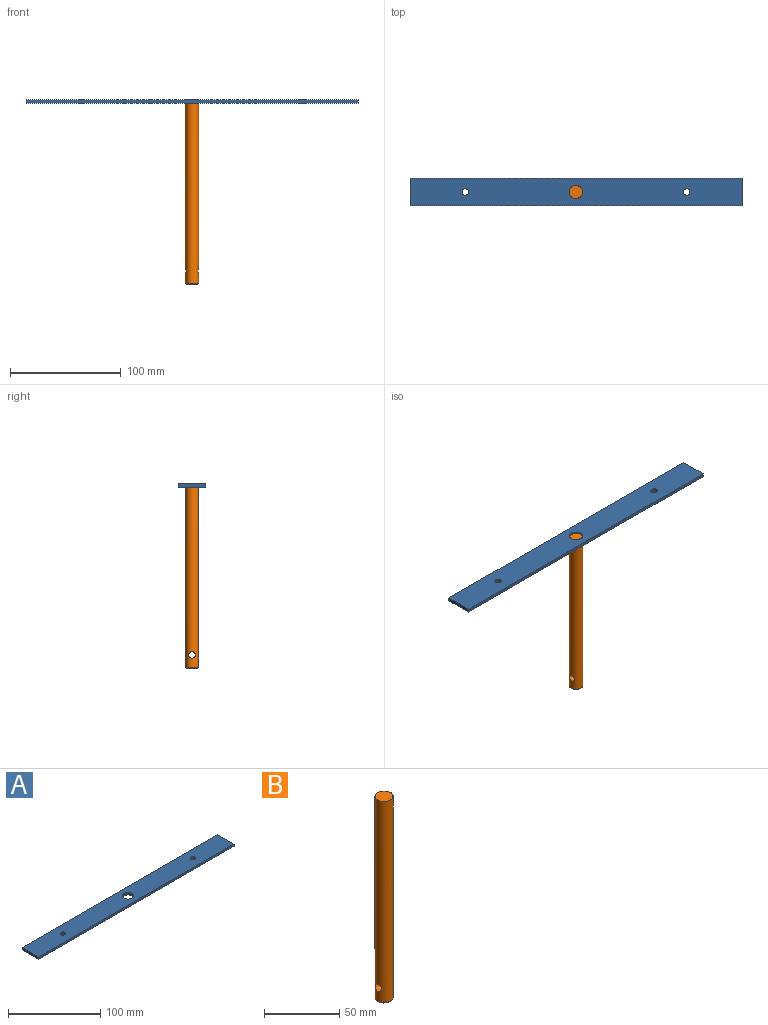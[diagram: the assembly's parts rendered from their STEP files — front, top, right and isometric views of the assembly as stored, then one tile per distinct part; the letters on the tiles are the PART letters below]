
ASSEMBLY  parts=2 mates=1
PART A: 9 faces, bbox 300x25x3 mm
  f0: plane 25x3mm, normal (1,0,0), area 75mm2, adj f1,f5,f7,f8
  f1: plane 300x3mm, normal (0,1,0), area 900mm2, adj f0,f2,f7,f8
  f2: plane 25x3mm, normal (-1,0,0), area 75mm2, adj f1,f5,f7,f8
  f3: cylinder r=3mm len=6mm, axis (0,0,-1), area 56.5mm2, adj f7,f8
  f4: cylinder r=6mm len=12mm, axis (0,0,-1), area 113.1mm2, adj f7,f8
  f5: plane 300x3mm, normal (0,-1,0), area 900mm2, adj f0,f2,f7,f8
  f6: cylinder r=3mm len=6mm, axis (0,0,-1), area 56.5mm2, adj f7,f8
  f7: plane 300x25mm, normal (0,0,1), area 7330.4mm2, adj f0,f1,f2,f3,f4,f5,f6
  f8: plane 300x25mm, normal (0,0,-1), area 7330.4mm2, adj f0,f1,f2,f3,f4,f5,f6
PART B: 5 faces, bbox 12x12x165 mm
  f0: cylinder r=6mm len=164mm, axis (0,0,1), area 6124.2mm2, adj f2,f3,f4
  f1: plane 10x10mm, normal (0,0,-1), area 78.5mm2, adj f4
  f2: plane 12x12mm, normal (0,0,1), area 113.1mm2, adj f0
  f3: cylinder r=3mm len=12mm, axis (1,0,0), area 211.3mm2, adj f0
  f4: cone r=5mm half-angle=45deg, axis (0,0,1), area 48.9mm2, adj f0,f1
PLACE A t=(-0.13,5.63,-54.97)mm
PLACE B t=(-0.13,5.63,-53.47)mm
MATE fastened A.f4 <-> B.f0  axis (0,0,-1) through (-0.13,28.13,51.53)mm
